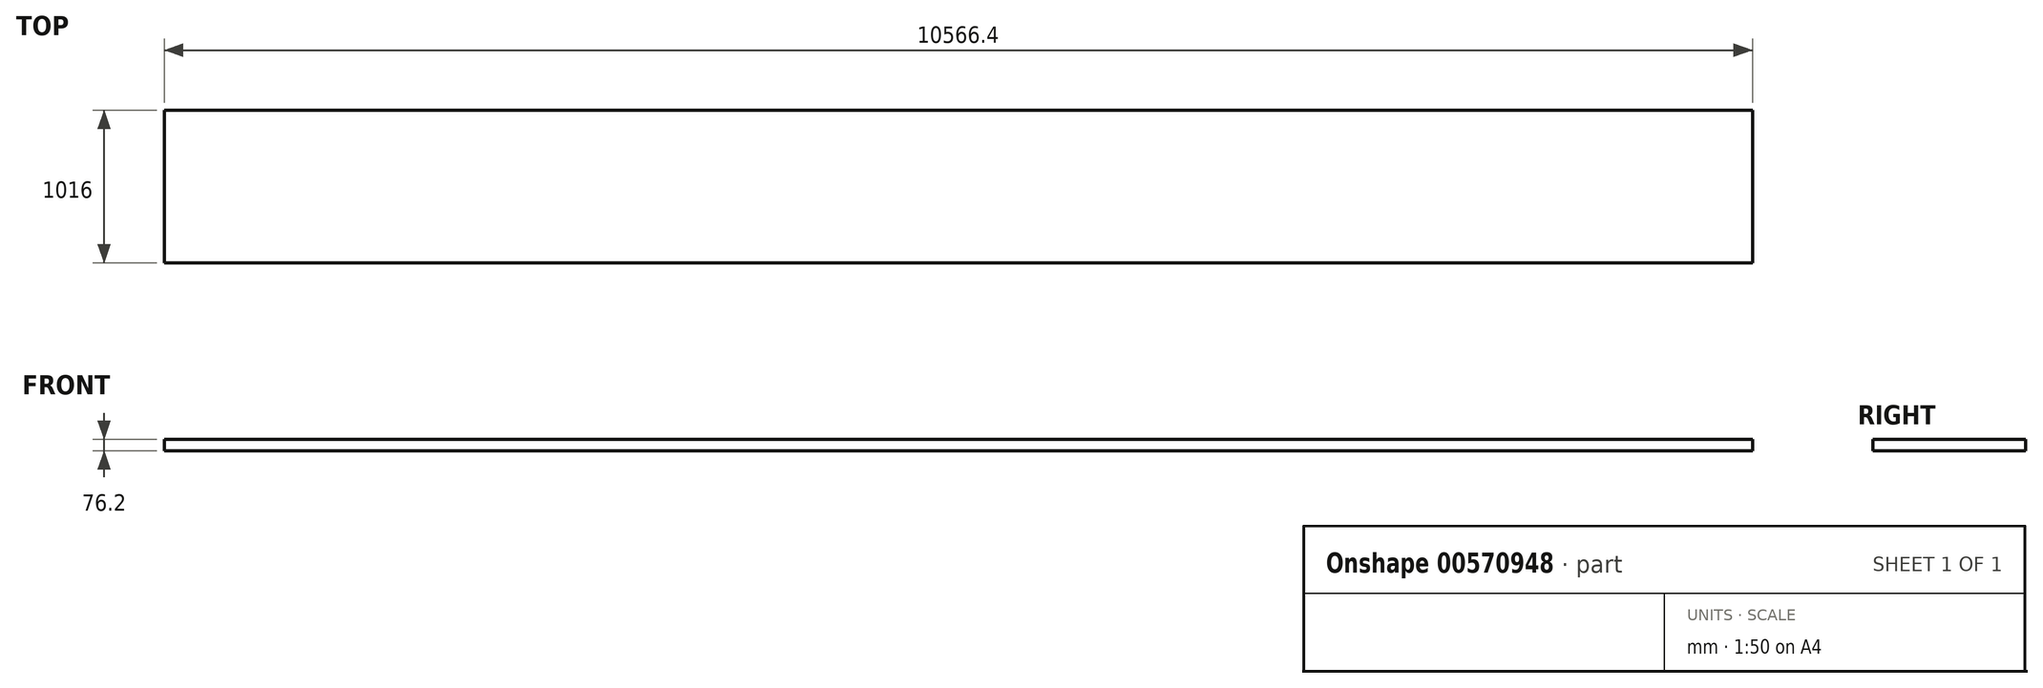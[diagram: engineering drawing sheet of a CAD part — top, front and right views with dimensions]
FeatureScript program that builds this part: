
annotation { "Feature Type Name" : "Feature", "Feature Type Description" : "" }
export const myFeature = defineFeature(function(context is Context, id is Id, definition is map)
    precondition{}
    {
        {
            var Q0;
            Q0=qCreatedBy(makeId("Top.planeOp"),FACE);
            var sketch = newSketch(context, id + "F0", { "sketchPlane" : qUnion([Q0])});
            skLineSegment(sketch, "E0.bottom", {"start": v(0, -508) * mm, "end": v(-10566.4, -508) * mm});
            skLineSegment(sketch, "E0.top", {"start": v(0, 508) * mm, "end": v(-10566.4, 508) * mm});
            skLineSegment(sketch, "E0.left", {"start": v(0, -508) * mm, "end": v(0, 508) * mm});
            skLineSegment(sketch, "E0.right", {"start": v(-10566.4, -508) * mm, "end": v(-10566.4, 508) * mm});
            skSolve(sketch);
        }
        {
            var Q0;
            Q0=makeQuery(id+"F0.imprint","IMPRINT",FACE,{"disambiguationData":[TD([[makeQuery(id+"F0.imprint","IMPRINT",EDGE,{"derivedFrom":sQuery(id+"F0.wireOp",EDGE,"E0.bottom")}),-1.0]])]});
            extrude(context, id + "F1", {"entities" : qUnion([Q0]), "oppositeDirection" : true, "depth" : 76.2 * mm, "offsetDistance" : 25.4 * mm});
        }
    });
